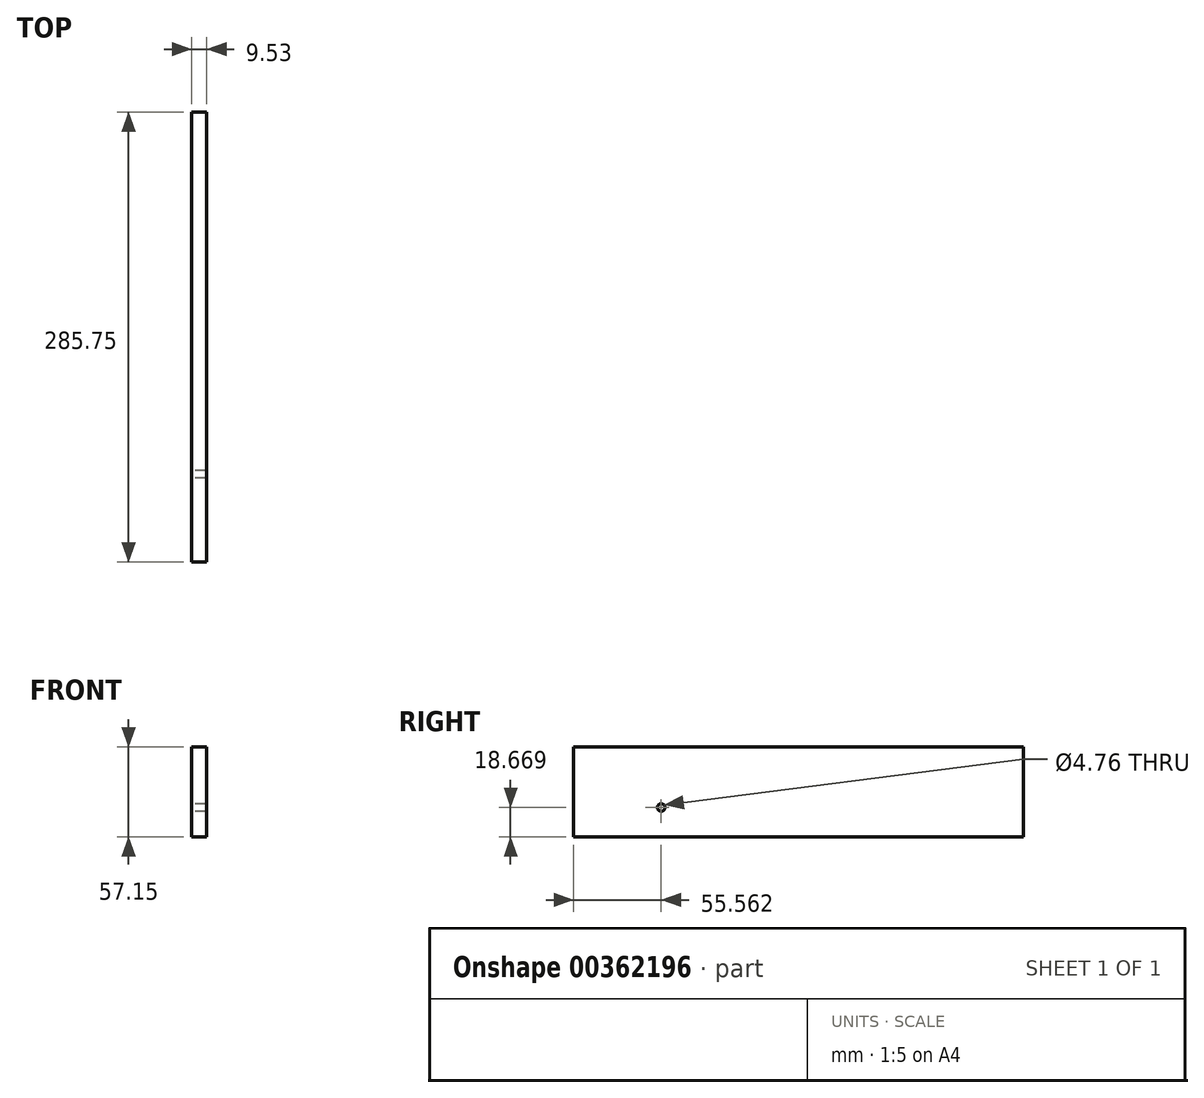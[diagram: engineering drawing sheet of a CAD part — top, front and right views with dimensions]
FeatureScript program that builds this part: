
annotation { "Feature Type Name" : "Feature", "Feature Type Description" : "" }
export const myFeature = defineFeature(function(context is Context, id is Id, definition is map)
    precondition{}
    {
        {
            var Q0;
            Q0=qCreatedBy(makeId("Right.planeOp"),FACE);
            var sketch = newSketch(context, id + "F0", { "sketchPlane" : qUnion([Q0])});
            skLineSegment(sketch, "E0.bottom", {"start": v(0, 0) * mm, "end": v(285.75, 0) * mm});
            skLineSegment(sketch, "E0.top", {"start": v(0, 57.15) * mm, "end": v(285.75, 57.15) * mm});
            skLineSegment(sketch, "E0.left", {"start": v(0, 0) * mm, "end": v(0, 57.15) * mm});
            skLineSegment(sketch, "E0.right", {"start": v(285.75, 0) * mm, "end": v(285.75, 57.15) * mm});
            skPoint(sketch, "E1", {"position": v(55.56, 18.67) * mm});
            skSolve(sketch);
        }
        {
            var Q0;
            Q0=makeQuery(id+"F0.imprint","IMPRINT",FACE,{"disambiguationData":[TD([[makeQuery(id+"F0.imprint","IMPRINT",EDGE,{"derivedFrom":sQuery(id+"F0.wireOp",EDGE,"E0.bottom")}),1.0]])]});
            extrude(context, id + "F1", {"entities" : qUnion([Q0]), "depth" : 9.52 * mm});
        }
        {
            var Q0;
            Q0=sQuery(id+"F0.wireOp",VERTEX,"E1");
            var Q1;
            Q1=makeQuery(id+"F1.opExtrude","SWEPT_BODY",BODY,{"disambiguationData":[OSD([sQuery(id+"F0.wireOp",EDGE,"E0.bottom"),sQuery(id+"F0.wireOp",EDGE,"E0.top"),sQuery(id+"F0.wireOp",EDGE,"E0.left"),sQuery(id+"F0.wireOp",EDGE,"E0.right")])]});
            hole(context, id + "F2", {"style" : HoleStyle.SIMPLE, "endStyle" : HoleEndStyle.THROUGH, "oppositeDirection" : true, "holeDiameter" : 4.76 * mm, "isTappedThrough" : true, "tappedDepth" : 12.7 * mm, "tapClearance" : 3, "startFromSketch" : true, "locations" : qUnion([Q0]), "scope" : qUnion([Q1])});
        }
    });
